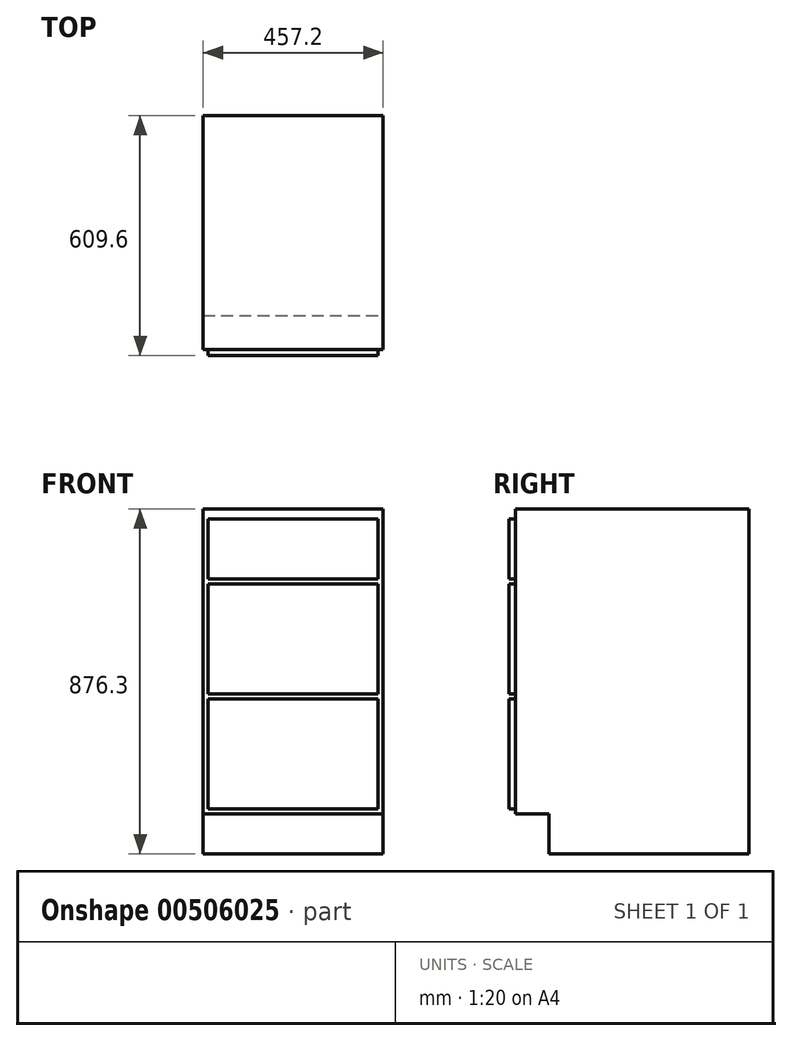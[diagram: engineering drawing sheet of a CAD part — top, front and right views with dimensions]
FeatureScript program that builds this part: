
annotation { "Feature Type Name" : "Feature", "Feature Type Description" : "" }
export const myFeature = defineFeature(function(context is Context, id is Id, definition is map)
    precondition{}
    {
        {
            var Q0;
            Q0=qCreatedBy(makeId("Top.planeOp"),FACE);
            var sketch = newSketch(context, id + "F0", { "sketchPlane" : qUnion([Q0])});
            skLineSegment(sketch, "E0.bottom", {"start": v(0, 0) * mm, "end": v(457.2, 0) * mm});
            skLineSegment(sketch, "E0.top", {"start": v(0, 609.6) * mm, "end": v(457.2, 609.6) * mm});
            skLineSegment(sketch, "E0.left", {"start": v(0, 0) * mm, "end": v(0, 609.6) * mm});
            skLineSegment(sketch, "E0.right", {"start": v(457.2, 0) * mm, "end": v(457.2, 609.6) * mm});
            skSolve(sketch);
        }
        {
            var Q0;
            Q0=makeQuery(id+"F0.imprint","IMPRINT",FACE,{"disambiguationData":[TD([[makeQuery(id+"F0.imprint","IMPRINT",EDGE,{"derivedFrom":sQuery(id+"F0.wireOp",EDGE,"E0.bottom")}),1.0]])]});
            extrude(context, id + "F1", {"entities" : qUnion([Q0]), "depth" : 876.3 * mm, "offsetDistance" : 25.4 * mm});
        }
        {
            var Q0;
            Q0=makeQuery(id+"F1.opExtrude","SWEPT_FACE",FACE,{"disambiguationData":[OSD([sQuery(id+"F0.wireOp",EDGE,"E0.bottom")])]});
            var sketch = newSketch(context, id + "F2", { "sketchPlane" : qUnion([Q0])});
            skLineSegment(sketch, "E1.bottom", {"start": v(457.2, 0) * mm, "end": v(0, 0) * mm});
            skLineSegment(sketch, "E1.top", {"start": v(457.2, 101.6) * mm, "end": v(0, 101.6) * mm});
            skLineSegment(sketch, "E1.left", {"start": v(457.2, 0) * mm, "end": v(457.2, 101.6) * mm});
            skLineSegment(sketch, "E1.right", {"start": v(0, 0) * mm, "end": v(0, 101.6) * mm});
            skSolve(sketch);
        }
        {
            var Q0;
            Q0 = qSketchRegion(id + "F2", true);
            extrude(context, id + "F3", {"entities" : qUnion([Q0]), "operationType" : NewBodyOperationType.REMOVE, "oppositeDirection" : true, "depth" : 101.6 * mm, "offsetDistance" : 25.4 * mm});
        }
        {
            var Q0;
            Q0=makeQuery(id+"F1.opExtrude","SWEPT_FACE",FACE,{"disambiguationData":[OSD([sQuery(id+"F0.wireOp",EDGE,"E0.bottom")])]});
            var sketch = newSketch(context, id + "F4", { "sketchPlane" : qUnion([Q0])});
            skLineSegment(sketch, "E2.bottom", {"start": v(12.7, 850.9) * mm, "end": v(444.5, 850.9) * mm});
            skLineSegment(sketch, "E2.top", {"start": v(12.7, 698.5) * mm, "end": v(444.5, 698.5) * mm});
            skLineSegment(sketch, "E2.left", {"start": v(12.7, 850.9) * mm, "end": v(12.7, 698.5) * mm});
            skLineSegment(sketch, "E2.right", {"start": v(444.5, 850.9) * mm, "end": v(444.5, 698.5) * mm});
            skLineSegment(sketch, "E3.bottom", {"start": v(12.7, 685.8) * mm, "end": v(444.5, 685.8) * mm});
            skLineSegment(sketch, "E3.top", {"start": v(12.7, 406.4) * mm, "end": v(444.5, 406.4) * mm});
            skLineSegment(sketch, "E3.left", {"start": v(12.7, 685.8) * mm, "end": v(12.7, 406.4) * mm});
            skLineSegment(sketch, "E3.right", {"start": v(444.5, 685.8) * mm, "end": v(444.5, 406.4) * mm});
            skLineSegment(sketch, "E4.bottom", {"start": v(12.7, 393.7) * mm, "end": v(444.5, 393.7) * mm});
            skLineSegment(sketch, "E4.top", {"start": v(12.7, 114.3) * mm, "end": v(444.5, 114.3) * mm});
            skLineSegment(sketch, "E4.left", {"start": v(12.7, 393.7) * mm, "end": v(12.7, 114.3) * mm});
            skLineSegment(sketch, "E4.right", {"start": v(444.5, 393.7) * mm, "end": v(444.5, 114.3) * mm});
            skLineSegment(sketch, "E5.bottom", {"start": v(457.2, 101.6) * mm, "end": v(0, 101.6) * mm});
            skLineSegment(sketch, "E5.top", {"start": v(457.2, 876.3) * mm, "end": v(0, 876.3) * mm});
            skLineSegment(sketch, "E5.left", {"start": v(457.2, 101.6) * mm, "end": v(457.2, 876.3) * mm});
            skLineSegment(sketch, "E5.right", {"start": v(0, 101.6) * mm, "end": v(0, 876.3) * mm});
            skSolve(sketch);
        }
        {
            var Q0;
            Q0=makeQuery(id+"F4.imprint","IMPRINT",FACE,{"disambiguationData":[TD([[makeQuery(id+"F4.imprint","IMPRINT",EDGE,{"derivedFrom":sQuery(id+"F4.wireOp",EDGE,"E2.bottom")}),1.0]])]});
            extrude(context, id + "F5", {"entities" : qUnion([Q0]), "operationType" : NewBodyOperationType.REMOVE, "oppositeDirection" : true, "depth" : 15.88 * mm, "offsetDistance" : 25.4 * mm});
        }
    });
